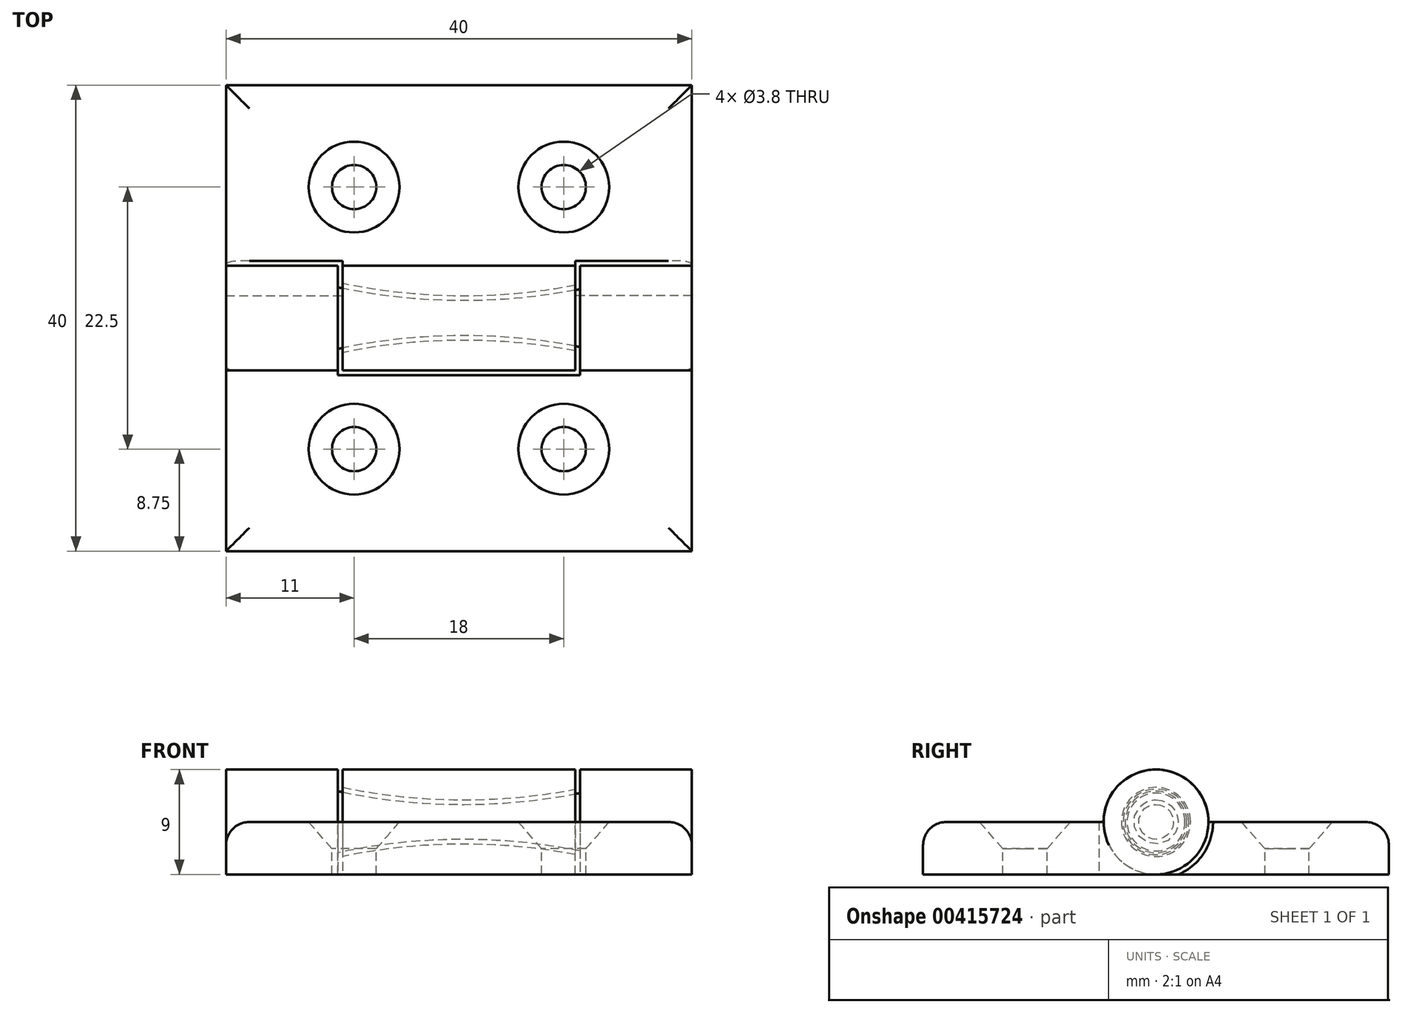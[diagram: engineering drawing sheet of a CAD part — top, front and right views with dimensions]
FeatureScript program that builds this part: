
annotation { "Feature Type Name" : "Feature", "Feature Type Description" : "" }
export const myFeature = defineFeature(function(context is Context, id is Id, definition is map)
    precondition{}
    {
        {
            assignVariable(context, id + "F0", {"name" : "GapSize", "anyValue" : .4});
        }
        {
            var Q0;
            Q0=qCreatedBy(makeId("Front.planeOp"),FACE);
            var sketch = newSketch(context, id + "F1", { "sketchPlane" : qUnion([Q0])});
            skLineSegment(sketch, "E0", {"start": v(-18.48, 0) * mm, "end": v(18.23, 0) * mm, "construction": true});
            skLineSegment(sketch, "E1", {"start": v(-10, 18.4) * mm, "end": v(-10, -18.31) * mm, "construction": true});
            skLineSegment(sketch, "E2", {"start": v(10, 18.4) * mm, "end": v(10, -18.31) * mm, "construction": true});
            skLineSegment(sketch, "E3.0", {"start": v(-18.48, 2) * mm, "end": v(18.23, 2) * mm, "construction": true});
            skLineSegment(sketch, "E4.0", {"start": v(-18.48, 1.5) * mm, "end": v(18.48, 1.5) * mm, "construction": true});
            skPoint(sketch, "E5", {"position": v(0, 1.5) * mm});
            skPoint(sketch, "E6", {"position": v(10, 2) * mm});
            skPoint(sketch, "E7", {"position": v(-10, 2) * mm});
            skArc(sketch, "E8", {"start": v(-10, 2) * mm, "mid": v(0, 1.5) * mm, "end": v(10, 2) * mm});
            skLineSegment(sketch, "E9", {"start": v(-10, 2) * mm, "end": v(-10, 0) * mm});
            skLineSegment(sketch, "E10", {"start": v(-10, 0) * mm, "end": v(10, 0) * mm});
            skLineSegment(sketch, "E11", {"start": v(10, 0) * mm, "end": v(10, 2) * mm});
            skSolve(sketch);
        }
        {
            var Q0;
            Q0=qCreatedBy(makeId("Front.planeOp"),FACE);
            var sketch = newSketch(context, id + "F2", { "sketchPlane" : qUnion([Q0])});
            skLineSegment(sketch, "E12.0", {"start": v(-10, 0) * mm, "end": v(10, 0) * mm});
            skLineSegment(sketch, "E13.0", {"start": v(-10, 2.56) * mm, "end": v(-10, 0) * mm});
            skLineSegment(sketch, "E14.0", {"start": v(10, 0) * mm, "end": v(10, 2.4) * mm});
            skLineSegment(sketch, "E15.0", {"start": v(10.4, 0) * mm, "end": v(10.4, 2.9) * mm});
            skArc(sketch, "E15.1", {"start": v(-10.4, 3.05) * mm, "mid": v(0, 1.9) * mm, "end": v(10.4, 2.9) * mm});
            skLineSegment(sketch, "E15.2", {"start": v(-10.4, 3.05) * mm, "end": v(-10.4, 0) * mm});
            skLineSegment(sketch, "E16", {"start": v(-10.4, 0) * mm, "end": v(-10, 0) * mm});
            skLineSegment(sketch, "E17", {"start": v(-10.4, 3.05) * mm, "end": v(-10.4, 4.5) * mm});
            skLineSegment(sketch, "E18", {"start": v(-10.4, 4.5) * mm, "end": v(10.4, 4.5) * mm});
            skLineSegment(sketch, "E19", {"start": v(10.4, 4.5) * mm, "end": v(10.4, 2.9) * mm});
            skLineSegment(sketch, "E20", {"start": v(-10, 2.97) * mm, "end": v(-10, 4.5) * mm});
            skLineSegment(sketch, "E21", {"start": v(10, 2.81) * mm, "end": v(10, 4.5) * mm});
            skArc(sketch, "E22.0", {"start": v(-10.4, 2.64) * mm, "mid": v(0, 1.5) * mm, "end": v(10.4, 2.48) * mm});
            skLineSegment(sketch, "E23", {"start": v(-10, 2.97) * mm, "end": v(-10, 2.56) * mm});
            skLineSegment(sketch, "E24", {"start": v(10, 2.81) * mm, "end": v(10, 2.4) * mm});
            skLineSegment(sketch, "E25", {"start": v(10.4, 0) * mm, "end": v(10, 0) * mm});
            skSolve(sketch);
        }
        {
            var Q0;
            Q0=makeQuery(id+"F2.imprint","IMPRINT",FACE,{"disambiguationData":[TD([[makeQuery(id+"F2.imprint","IMPRINT",EDGE,{"derivedFrom":sQuery(id+"F2.wireOp",EDGE,"E12.0")}),1.0]])]});
            var Q1;
            {var subQ0=sQuery(id+"F2.wireOp",EDGE,"E13.0");Q1=makeQuery(id+"F2.imprint","IMPRINT",FACE,{"disambiguationData":[TD([[makeQuery(id+"F2.imprint","IMPRINT",EDGE,{"derivedFrom":subQ0}),-1.0]])]});}
            var Q2;
            {var subQ0=sQuery(id+"F2.wireOp",EDGE,"E14.0");Q2=makeQuery(id+"F2.imprint","IMPRINT",FACE,{"disambiguationData":[TD([[makeQuery(id+"F2.imprint","IMPRINT",EDGE,{"derivedFrom":subQ0}),-1.0]])]});}
            var Q3;
            Q3=sQuery(id+"F2.wireOp",EDGE,"E12.0");
            revolve(context, id + "F3", {"entities" : qUnion([Q0, Q1, Q2]), "axis" : qUnion([Q3]), "revolveType" : RevolveType.FULL});
        }
        {
            var Q0;
            {var subQ0=sQuery(id+"F2.wireOp",EDGE,"E20");Q0=makeQuery(id+"F2.imprint","IMPRINT",FACE,{"disambiguationData":[TD([[makeQuery(id+"F2.imprint","IMPRINT",EDGE,{"derivedFrom":subQ0}),-1.0]])]});}
            var Q1;
            Q1=sQuery(id+"F2.wireOp",EDGE,"E12.0");
            revolve(context, id + "F4", {"entities" : qUnion([Q0]), "axis" : qUnion([Q1]), "revolveType" : RevolveType.FULL});
        }
        {
            var Q0;
            Q0=qCreatedBy(makeId("Right.planeOp"),FACE);
            var sketch = newSketch(context, id + "F5", { "sketchPlane" : qUnion([Q0])});
            skPoint(sketch, "E26", {"position": v(4.5, 0) * mm});
            skLineSegment(sketch, "E27.0", {"start": v(-20, 18.4) * mm, "end": v(-20, -18.31) * mm, "construction": true});
            skLineSegment(sketch, "E28", {"start": v(-23.98, 0) * mm, "end": v(20, 0) * mm, "construction": true});
            skLineSegment(sketch, "E29.0", {"start": v(-23.98, -4.5) * mm, "end": v(20, -4.5) * mm, "construction": true});
            skPoint(sketch, "E30", {"position": v(-20, 0) * mm});
            skPoint(sketch, "E31", {"position": v(-20, -4.5) * mm});
            skPoint(sketch, "E32", {"position": v(4.5, -4.5) * mm});
            skLineSegment(sketch, "E33", {"start": v(-20, 0) * mm, "end": v(-20, -4.5) * mm});
            skLineSegment(sketch, "E34", {"start": v(4.5, -4.5) * mm, "end": v(4.5, 0) * mm});
            skLineSegment(sketch, "E35", {"start": v(-20, 0) * mm, "end": v(4.5, 0) * mm});
            skLineSegment(sketch, "E36", {"start": v(4.5, -4.5) * mm, "end": v(-20, -4.5) * mm});
            skLineSegment(sketch, "E37.0", {"start": v(20, 18.4) * mm, "end": v(20, -18.31) * mm, "construction": true});
            skPoint(sketch, "E38", {"position": v(-4.5, 0) * mm});
            skPoint(sketch, "E39", {"position": v(-20.6, 23.68) * mm});
            skLineSegment(sketch, "E40", {"start": v(-4.5, 0) * mm, "end": v(-4.5, -4.5) * mm});
            skLineSegment(sketch, "E41", {"start": v(4.5, 0) * mm, "end": v(20, 0) * mm});
            skLineSegment(sketch, "E42", {"start": v(20, -4.5) * mm, "end": v(20, 0) * mm});
            skLineSegment(sketch, "E43", {"start": v(20, -4.5) * mm, "end": v(4.5, -4.5) * mm});
            skCircle(sketch, "E44.0", {"center": v(0, 0) * mm, "radius": 4.5 * mm});
            skSolve(sketch);
        }
        {
            var Q0;
            Q0=qCreatedBy(makeId("Right.planeOp"),FACE);
            cPlane(context, id + "F6", {"entities" : qUnion([Q0]), "cplaneType" : CPlaneType.OFFSET, "offset" : 20 * mm, "width" : 150 * mm, "height" : 150 * mm});
        }
        {
            var Q0;
            Q0=qCreatedBy(makeId("Right.planeOp"),FACE);
            cPlane(context, id + "F7", {"entities" : qUnion([Q0]), "cplaneType" : CPlaneType.OFFSET, "offset" : 20 * mm, "oppositeDirection" : true, "width" : 150 * mm, "height" : 150 * mm});
        }
        {
            var Q0;
            Q0=makeQuery(id+"F5.imprint","IMPRINT",FACE,{"disambiguationData":[TD([[makeQuery(id+"F5.imprint","IMPRINT",EDGE,{"derivedFrom":sQuery(id+"F5.wireOp",EDGE,"E34")}),-1.0]])]});
            var Q1;
            {var subQ0=sQuery(id+"F5.wireOp",EDGE,"E34");Q1=makeQuery(id+"F5.imprint","IMPRINT",FACE,{"disambiguationData":[TD([[makeQuery(id+"F5.imprint","IMPRINT",EDGE,{"derivedFrom":subQ0}),1.0]])]});}
            var Q2;
            Q2=makeQuery(id+"F4.opRevolve","SWEPT_FACE",FACE,{"disambiguationData":[OSD([sQuery(id+"F2.wireOp",EDGE,"E21")])]});
            var Q3;
            Q3=makeQuery(id+"F4.opRevolve","SWEPT_FACE",FACE,{"disambiguationData":[OSD([sQuery(id+"F2.wireOp",EDGE,"E20")])]});
            extrude(context, id + "F8", {"entities" : qUnion([Q0, Q1]), "operationType" : NewBodyOperationType.ADD, "endBound" : BoundingType.UP_TO_SURFACE, "endBoundEntityFace" : qUnion([Q2]), "depth" : 25 * mm, "hasSecondDirection" : true, "secondDirectionBound" : SecondDirectionBoundingType.UP_TO_SURFACE, "secondDirectionOppositeDirection" : true, "secondDirectionBoundEntityFace" : qUnion([Q3]), "secondDirectionDepth" : 25 * mm});
        }
        {
            var Q0;
            Q0=qCreatedBy(id+"F6.planeOp",FACE);
            var sketch = newSketch(context, id + "F9", { "sketchPlane" : qUnion([Q0])});
            skLineSegment(sketch, "E45.0", {"start": v(-20, 0) * mm, "end": v(4.5, 0) * mm});
            skLineSegment(sketch, "E46.0", {"start": v(-4.5, 0) * mm, "end": v(-4.5, -4.5) * mm});
            skLineSegment(sketch, "E47.0", {"start": v(4.5, -4.5) * mm, "end": v(-20, -4.5) * mm});
            skLineSegment(sketch, "E48.0", {"start": v(-20, 0) * mm, "end": v(-20, -4.5) * mm});
            skCircle(sketch, "E49.0", {"center": v(0, 0) * mm, "radius": 4.5 * mm});
            skLineSegment(sketch, "E50.0", {"start": v(-4.9, 0) * mm, "end": v(-4.9, -4.5) * mm});
            skSolve(sketch);
        }
        {
            var Q0;
            {var subQ0=sQuery(id+"F9.wireOp",EDGE,"E49.0");var subQ1=sQuery(id+"F9.wireOp",EDGE,"E45.0");var subQ2=makeQuery(id+"F9.imprint","INTERSECT",VERTEX,{"derivedFrom":[subQ1,subQ0]});Q0=makeQuery(id+"F9.imprint","IMPRINT",FACE,{"disambiguationData":[TD([[makeQuery(id+"F9.imprint","IMPRINT",EDGE,{"disambiguationData":[TD([[subQ2,1.0]])],"derivedFrom":subQ1}),1.0]])]});}
            var Q1;
            {var subQ0=sQuery(id+"F9.wireOp",EDGE,"E49.0");var subQ1=sQuery(id+"F9.wireOp",EDGE,"E45.0");var subQ2=makeQuery(id+"F9.imprint","INTERSECT",VERTEX,{"derivedFrom":[subQ1,subQ0]});Q1=makeQuery(id+"F9.imprint","IMPRINT",FACE,{"disambiguationData":[TD([[makeQuery(id+"F9.imprint","IMPRINT",EDGE,{"disambiguationData":[TD([[subQ2,1.0]])],"derivedFrom":subQ0}),1.0]])]});}
            var Q2;
            {var subQ0=sQuery(id+"F9.wireOp",EDGE,"E46.0");Q2=makeQuery(id+"F9.imprint","IMPRINT",FACE,{"disambiguationData":[TD([[makeQuery(id+"F9.imprint","IMPRINT",EDGE,{"derivedFrom":subQ0}),1.0]])]});}
            var Q3;
            Q3=makeQuery(id+"F3.opRevolve","SWEPT_FACE",FACE,{"disambiguationData":[OSD([sQuery(id+"F2.wireOp",EDGE,"E15.0")])]});
            extrude(context, id + "F10", {"entities" : qUnion([Q0, Q1, Q2]), "operationType" : NewBodyOperationType.ADD, "endBound" : BoundingType.UP_TO_SURFACE, "oppositeDirection" : true, "endBoundEntityFace" : qUnion([Q3]), "depth" : 25 * mm});
        }
        {
            var Q0;
            Q0=qCreatedBy(id+"F7.planeOp",FACE);
            var sketch = newSketch(context, id + "F11", { "sketchPlane" : qUnion([Q0])});
            skCircle(sketch, "E51.0", {"center": v(0, 0) * mm, "radius": 4.5 * mm});
            skLineSegment(sketch, "E52.0", {"start": v(4.5, -4.5) * mm, "end": v(-20, -4.5) * mm});
            skLineSegment(sketch, "E53.0", {"start": v(-4.5, 0) * mm, "end": v(-4.5, -4.5) * mm});
            skLineSegment(sketch, "E54.0", {"start": v(-20, 0) * mm, "end": v(-20, -4.5) * mm});
            skLineSegment(sketch, "E55.0", {"start": v(-20, 0) * mm, "end": v(4.5, 0) * mm});
            skLineSegment(sketch, "E56.0", {"start": v(-4.9, 0) * mm, "end": v(-4.9, -4.5) * mm});
            skSolve(sketch);
        }
        {
            var Q0;
            {var subQ0=sQuery(id+"F11.wireOp",EDGE,"E55.0");var subQ1=sQuery(id+"F11.wireOp",EDGE,"E51.0");var subQ2=makeQuery(id+"F11.imprint","INTERSECT",VERTEX,{"derivedFrom":[subQ1,subQ0]});Q0=makeQuery(id+"F11.imprint","IMPRINT",FACE,{"disambiguationData":[TD([[makeQuery(id+"F11.imprint","IMPRINT",EDGE,{"disambiguationData":[TD([[subQ2,1.0]])],"derivedFrom":subQ1}),1.0]])]});}
            var Q1;
            {var subQ0=sQuery(id+"F11.wireOp",EDGE,"E55.0");var subQ1=sQuery(id+"F11.wireOp",EDGE,"E51.0");var subQ3=makeQuery(id+"F11.imprint","INTERSECT",VERTEX,{"derivedFrom":[subQ1,subQ0]});Q1=makeQuery(id+"F11.imprint","IMPRINT",FACE,{"disambiguationData":[TD([[makeQuery(id+"F11.imprint","IMPRINT",EDGE,{"disambiguationData":[TD([[subQ3,-1.0]])],"derivedFrom":subQ1}),1.0]])]});}
            var Q2;
            {var subQ0=sQuery(id+"F11.wireOp",EDGE,"E53.0");Q2=makeQuery(id+"F11.imprint","IMPRINT",FACE,{"disambiguationData":[TD([[makeQuery(id+"F11.imprint","IMPRINT",EDGE,{"derivedFrom":subQ0}),1.0]])]});}
            var Q3;
            Q3=makeQuery(id+"F3.opRevolve","SWEPT_FACE",FACE,{"disambiguationData":[OSD([sQuery(id+"F2.wireOp",EDGE,"E15.2")])]});
            extrude(context, id + "F12", {"entities" : qUnion([Q0, Q1, Q2]), "operationType" : NewBodyOperationType.ADD, "endBound" : BoundingType.UP_TO_SURFACE, "endBoundEntityFace" : qUnion([Q3]), "depth" : 25 * mm});
        }
        {
            var Q0;
            {var subQ0=sQuery(id+"F9.wireOp",EDGE,"E46.0");Q0=makeQuery(id+"F9.imprint","IMPRINT",FACE,{"disambiguationData":[TD([[makeQuery(id+"F9.imprint","IMPRINT",EDGE,{"derivedFrom":subQ0}),-1.0]])]});}
            var Q1;
            Q1=makeQuery(id+"F15.opExtrude","SWEPT_FACE",FACE,{"disambiguationData":[OSD([sQuery(id+"F9.wireOp",EDGE,"E50.0")])]});
            extrude(context, id + "F13", {"entities" : qUnion([Q0]), "operationType" : NewBodyOperationType.ADD, "oppositeDirection" : true, "endBoundEntityFace" : qUnion([Q1]), "depth" : (10 - getVariable(context, 'GapSize')) * mm});
        }
        {
            var Q0;
            {var subQ0=sQuery(id+"F11.wireOp",EDGE,"E53.0");Q0=makeQuery(id+"F11.imprint","IMPRINT",FACE,{"disambiguationData":[TD([[makeQuery(id+"F11.imprint","IMPRINT",EDGE,{"derivedFrom":subQ0}),-1.0]])]});}
            extrude(context, id + "F14", {"entities" : qUnion([Q0]), "operationType" : NewBodyOperationType.ADD, "depth" : (10 - getVariable(context, 'GapSize')) * mm});
        }
        {
            var Q0;
            {var subQ0=sQuery(id+"F9.wireOp",EDGE,"E48.0");Q0=makeQuery(id+"F9.imprint","IMPRINT",FACE,{"disambiguationData":[TD([[makeQuery(id+"F9.imprint","IMPRINT",EDGE,{"derivedFrom":subQ0}),1.0]])]});}
            var Q1;
            {var subQ0=sQuery(id+"F11.wireOp",EDGE,"E53.0");var subQ1=sQuery(id+"F11.wireOp",EDGE,"E52.0");Q1=makeQuery(id+"F14.boolean.opBoolean","MERGE",FACE,{"derivedFrom":[makeQuery(id+"F12.opExtrude","CAP_FACE",FACE,{"disambiguationData":[OSD([sQuery(id+"F11.wireOp",EDGE,"E51.0"),subQ1,subQ0])],"isStart":true}),makeQuery(id+"F14.opExtrude","CAP_FACE",FACE,{"disambiguationData":[OSD([subQ1,subQ0,sQuery(id+"F11.wireOp",EDGE,"E55.0"),sQuery(id+"F11.wireOp",EDGE,"E56.0")])],"isStart":true})]});}
            extrude(context, id + "F15", {"entities" : qUnion([Q0]), "operationType" : NewBodyOperationType.ADD, "endBound" : BoundingType.UP_TO_SURFACE, "oppositeDirection" : true, "endBoundEntityFace" : qUnion([Q1]), "depth" : 40 * mm});
        }
        {
            var Q0;
            Q0=makeQuery(id+"F8.boolean.opBoolean","MERGE",FACE,{"derivedFrom":[makeQuery(id+"F4.opRevolve","SWEPT_FACE",FACE,{"disambiguationData":[OSD([sQuery(id+"F2.wireOp",EDGE,"E20")])]}),makeQuery(id+"F8.opExtrude","CAP_FACE",FACE,{"disambiguationData":[OSD([sQuery(id+"F5.wireOp",EDGE,"E36"),sQuery(id+"F5.wireOp",EDGE,"E41"),sQuery(id+"F5.wireOp",EDGE,"E42"),sQuery(id+"F5.wireOp",EDGE,"E43"),sQuery(id+"F5.wireOp",EDGE,"E44.0")])],"isStart":true})]});
            var sketch = newSketch(context, id + "F16", { "sketchPlane" : qUnion([Q0])});
            skCircle(sketch, "E57.0", {"center": v(0, 0) * mm, "radius": 4.9 * mm});
            skSolve(sketch);
        }
        {
            var Q0;
            {var subQ5=makeQuery(id+"F8.opExtrude","CAP_EDGE",EDGE,{"disambiguationData":[OSD([sQuery(id+"F5.wireOp",EDGE,"E42")])],"isStart":true});Q0=makeQuery(id+"F16.imprint","IMPRINT",FACE,{"disambiguationData":[TD([[makeQuery(id+"F16.imprint","IMPRINT",EDGE,{"derivedFrom":subQ5}),1.0]])]});}
            var Q1;
            {var subQ0=sQuery(id+"F11.wireOp",EDGE,"E53.0");var subQ1=sQuery(id+"F11.wireOp",EDGE,"E52.0");Q1=makeQuery(id+"F15.boolean.opBoolean","MERGE",FACE,{"derivedFrom":[makeQuery(id+"F14.boolean.opBoolean","MERGE",FACE,{"derivedFrom":[makeQuery(id+"F12.opExtrude","CAP_FACE",FACE,{"disambiguationData":[OSD([sQuery(id+"F11.wireOp",EDGE,"E51.0"),subQ1,subQ0])],"isStart":true}),makeQuery(id+"F14.opExtrude","CAP_FACE",FACE,{"disambiguationData":[OSD([subQ1,subQ0,sQuery(id+"F11.wireOp",EDGE,"E55.0"),sQuery(id+"F11.wireOp",EDGE,"E56.0")])],"isStart":true})]}),makeQuery(id+"F15.opExtrude","CAP_FACE",FACE,{"disambiguationData":[OSD([sQuery(id+"F9.wireOp",EDGE,"E45.0"),sQuery(id+"F9.wireOp",EDGE,"E47.0"),sQuery(id+"F9.wireOp",EDGE,"E48.0"),sQuery(id+"F9.wireOp",EDGE,"E50.0")])],"isStart":false})]});}
            extrude(context, id + "F17", {"entities" : qUnion([Q0]), "operationType" : NewBodyOperationType.ADD, "endBound" : BoundingType.UP_TO_SURFACE, "endBoundEntityFace" : qUnion([Q1]), "depth" : 25 * mm});
        }
        {
            var Q0;
            Q0=makeQuery(id+"F8.boolean.opBoolean","MERGE",FACE,{"derivedFrom":[makeQuery(id+"F4.opRevolve","SWEPT_FACE",FACE,{"disambiguationData":[OSD([sQuery(id+"F2.wireOp",EDGE,"E21")])]}),makeQuery(id+"F8.opExtrude","CAP_FACE",FACE,{"disambiguationData":[OSD([sQuery(id+"F5.wireOp",EDGE,"E36"),sQuery(id+"F5.wireOp",EDGE,"E41"),sQuery(id+"F5.wireOp",EDGE,"E42"),sQuery(id+"F5.wireOp",EDGE,"E43"),sQuery(id+"F5.wireOp",EDGE,"E44.0")])],"isStart":false})]});
            var sketch = newSketch(context, id + "F18", { "sketchPlane" : qUnion([Q0])});
            skCircle(sketch, "E58.0", {"center": v(0, 0) * mm, "radius": 4.9 * mm});
            skSolve(sketch);
        }
        {
            var Q0;
            {var subQ5=makeQuery(id+"F8.opExtrude","CAP_EDGE",EDGE,{"disambiguationData":[OSD([sQuery(id+"F5.wireOp",EDGE,"E42")])],"isStart":false});Q0=makeQuery(id+"F18.imprint","IMPRINT",FACE,{"disambiguationData":[TD([[makeQuery(id+"F18.imprint","IMPRINT",EDGE,{"derivedFrom":subQ5}),-1.0]])]});}
            var Q1;
            {var subQ0=sQuery(id+"F9.wireOp",EDGE,"E50.0");var subQ1=sQuery(id+"F9.wireOp",EDGE,"E47.0");var subQ2=sQuery(id+"F9.wireOp",EDGE,"E45.0");var subQ3=sQuery(id+"F9.wireOp",EDGE,"E46.0");Q1=makeQuery(id+"F15.boolean.opBoolean","MERGE",FACE,{"derivedFrom":[makeQuery(id+"F13.boolean.opBoolean","MERGE",FACE,{"derivedFrom":[makeQuery(id+"F10.opExtrude","CAP_FACE",FACE,{"disambiguationData":[OSD([subQ3,subQ1,sQuery(id+"F9.wireOp",EDGE,"E49.0")])],"isStart":true}),makeQuery(id+"F13.opExtrude","CAP_FACE",FACE,{"disambiguationData":[OSD([subQ2,subQ3,subQ1,subQ0])],"isStart":true})]}),makeQuery(id+"F15.opExtrude","CAP_FACE",FACE,{"disambiguationData":[OSD([subQ2,subQ1,sQuery(id+"F9.wireOp",EDGE,"E48.0"),subQ0])],"isStart":true})]});}
            extrude(context, id + "F19", {"entities" : qUnion([Q0]), "operationType" : NewBodyOperationType.ADD, "endBound" : BoundingType.UP_TO_SURFACE, "endBoundEntityFace" : qUnion([Q1]), "depth" : 25 * mm});
        }
        {
            var Q0;
            Q0=makeQuery(id+"F15.opExtrude","CAP_EDGE",EDGE,{"disambiguationData":[OSD([sQuery(id+"F5.wireOp",EDGE,"E35")])],"isStart":true});
            var Q1;
            Q1=makeQuery(id+"F15.opExtrude","SWEPT_EDGE",EDGE,{"disambiguationData":[OSD([sQuery(id+"F5.wireOp",EDGE,"E33"),sQuery(id+"F5.wireOp",EDGE,"E35")])]});
            var Q2;
            Q2=makeQuery(id+"F15.opExtrude","CAP_EDGE",EDGE,{"disambiguationData":[OSD([sQuery(id+"F5.wireOp",EDGE,"E35")])],"isStart":false});
            var Q3;
            Q3=makeQuery(id+"F19.opExtrude","CAP_EDGE",EDGE,{"disambiguationData":[OSD([sQuery(id+"F5.wireOp",EDGE,"E41")])],"isStart":false});
            var Q4;
            {var subQ0=sQuery(id+"F5.wireOp",EDGE,"E42");var subQ1=sQuery(id+"F5.wireOp",EDGE,"E41");Q4=makeQuery(id+"F19.boolean.opBoolean","MERGE",EDGE,{"derivedFrom":[makeQuery(id+"F17.boolean.opBoolean","MERGE",EDGE,{"derivedFrom":[makeQuery(id+"F8.opExtrude","TWEAK_EDGE",EDGE,{"derivedFrom":[makeQuery(id+"F5.imprint","IMPRINT",EDGE,{"derivedFrom":subQ1}),makeQuery(id+"F5.imprint","IMPRINT",EDGE,{"derivedFrom":subQ0})]}),makeQuery(id+"F17.opExtrude","SWEPT_EDGE",EDGE,{"disambiguationData":[OSD([subQ1,subQ0])]})]}),makeQuery(id+"F19.opExtrude","SWEPT_EDGE",EDGE,{"disambiguationData":[OSD([subQ1,subQ0])]})]});}
            var Q5;
            Q5=makeQuery(id+"F17.opExtrude","CAP_EDGE",EDGE,{"disambiguationData":[OSD([sQuery(id+"F5.wireOp",EDGE,"E41")])],"isStart":false});
            var Q6;
            Q6=makeQuery(id+"F15.boolean.opBoolean","MERGE",EDGE,{"derivedFrom":[makeQuery(id+"F14.opExtrude","CAP_EDGE",EDGE,{"disambiguationData":[OSD([sQuery(id+"F11.wireOp",EDGE,"E55.0")])],"isStart":true}),makeQuery(id+"F15.opExtrude","CAP_EDGE",EDGE,{"disambiguationData":[OSD([sQuery(id+"F9.wireOp",EDGE,"E45.0")])],"isStart":false})]});
            var Q7;
            Q7=makeQuery(id+"F15.opExtrude","SWEPT_EDGE",EDGE,{"disambiguationData":[OSD([sQuery(id+"F9.wireOp",EDGE,"E45.0"),sQuery(id+"F9.wireOp",EDGE,"E48.0")])]});
            var Q8;
            {var subQ0=sQuery(id+"F9.wireOp",EDGE,"E45.0");Q8=makeQuery(id+"F15.boolean.opBoolean","MERGE",EDGE,{"derivedFrom":[makeQuery(id+"F13.opExtrude","CAP_EDGE",EDGE,{"disambiguationData":[OSD([subQ0])],"isStart":true}),makeQuery(id+"F15.opExtrude","CAP_EDGE",EDGE,{"disambiguationData":[OSD([subQ0])],"isStart":true})]});}
            fillet(context, id + "F20", {"entities" : qUnion([Q0, Q1, Q2, Q3, Q4, Q5, Q6, Q7, Q8]), "radius" : 2 * mm, "allowEdgeOverflow" : false});
        }
        {
            var Q0;
            {var subQ0=sQuery(id+"F9.wireOp",EDGE,"E45.0");Q0=makeQuery(id+"F15.boolean.opBoolean","MERGE",FACE,{"derivedFrom":[makeQuery(id+"F13.opExtrude","SWEPT_FACE",FACE,{"disambiguationData":[OSD([subQ0])]}),makeQuery(id+"F14.opExtrude","SWEPT_FACE",FACE,{"disambiguationData":[OSD([sQuery(id+"F11.wireOp",EDGE,"E55.0")])]}),makeQuery(id+"F15.opExtrude","SWEPT_FACE",FACE,{"disambiguationData":[OSD([subQ0])]})]});}
            var sketch = newSketch(context, id + "F21", { "sketchPlane" : qUnion([Q0])});
            skLineSegment(sketch, "E59.0", {"start": v(-18, -4.5) * mm, "end": v(-18, -18) * mm});
            skLineSegment(sketch, "E60.0", {"start": v(-18, 18) * mm, "end": v(-18, 4.9) * mm});
            skLineSegment(sketch, "E61.0", {"start": v(-20, 20) * mm, "end": v(20, 20) * mm});
            skLineSegment(sketch, "E62.0", {"start": v(10, 4.5) * mm, "end": v(-10, 4.5) * mm});
            skLineSegment(sketch, "E63.0", {"start": v(-10.4, -4.9) * mm, "end": v(10.4, -4.9) * mm});
            skLineSegment(sketch, "E64.0", {"start": v(18, 18) * mm, "end": v(-18, 18) * mm});
            skLineSegment(sketch, "E65", {"start": v(9, 4.5) * mm, "end": v(9, 18) * mm, "construction": true});
            skPoint(sketch, "E66.startSnap0", {"position": v(0, 18) * mm});
            skLineSegment(sketch, "E67.0", {"start": v(18, 4.9) * mm, "end": v(18, 18) * mm});
            skLineSegment(sketch, "E68", {"start": v(0, 11.25) * mm, "end": v(18, 11.25) * mm, "construction": true});
            skPoint(sketch, "E68.startSnap0", {"position": v(9, 11.25) * mm});
            skPoint(sketch, "E69.MirrorP", {"position": v(-9, 11.25) * mm});
            skPoint(sketch, "E70.MirrorP", {"position": v(-9, -11.25) * mm});
            skPoint(sketch, "E71.MirrorP", {"position": v(9, -11.25) * mm});
            skSolve(sketch);
        }
        {
            var Q0;
            Q0=sQuery(id+"F21.wireOp",VERTEX,"E68.startSnap0");
            var Q1;
            Q1=sQuery(id+"F21.wireOp",VERTEX,"E69.MirrorP");
            var Q2;
            Q2=sQuery(id+"F21.wireOp",VERTEX,"E70.MirrorP");
            var Q3;
            Q3=sQuery(id+"F21.wireOp",VERTEX,"E71.MirrorP");
            var Q4;
            Q4=makeQuery(id+"F3.opRevolve","SWEPT_BODY",BODY,{"disambiguationData":[OSD([sQuery(id+"F2.wireOp",EDGE,"E12.0"),sQuery(id+"F2.wireOp",EDGE,"E15.0"),sQuery(id+"F2.wireOp",EDGE,"E15.2"),sQuery(id+"F2.wireOp",EDGE,"E16"),sQuery(id+"F2.wireOp",EDGE,"E22.0"),sQuery(id+"F2.wireOp",EDGE,"E25")])]});
            var Q5;
            Q5=makeQuery(id+"F4.opRevolve","SWEPT_BODY",BODY,{"disambiguationData":[OSD([sQuery(id+"F2.wireOp",EDGE,"E15.1"),sQuery(id+"F2.wireOp",EDGE,"E18"),sQuery(id+"F2.wireOp",EDGE,"E20"),sQuery(id+"F2.wireOp",EDGE,"E21")])]});
            hole(context, id + "F22", {"style" : HoleStyle.C_SINK, "endStyle" : HoleEndStyle.THROUGH, "standardTappedOrClearance" : lookupTablePath({ "standard" : "ANSI", "fit" : "Normal (ASME)", "size" : "#6", "type" : "Clearance" }), "standardBlindInLast" : lookupTablePath({ "fit" : "Free", "standard" : "ANSI", "size" : "#6", "type" : "Clearance" }), "holeDiameter" : 3.8 * mm, "cSinkDiameter" : 7.8 * mm, "cSinkAngle" : 82 * degree, "isTappedThrough" : true, "tappedDepth" : 12 * mm, "tapClearance" : 3, "locations" : qUnion([Q0, Q1, Q2, Q3]), "scope" : qUnion([Q4, Q5])});
        }
    });
